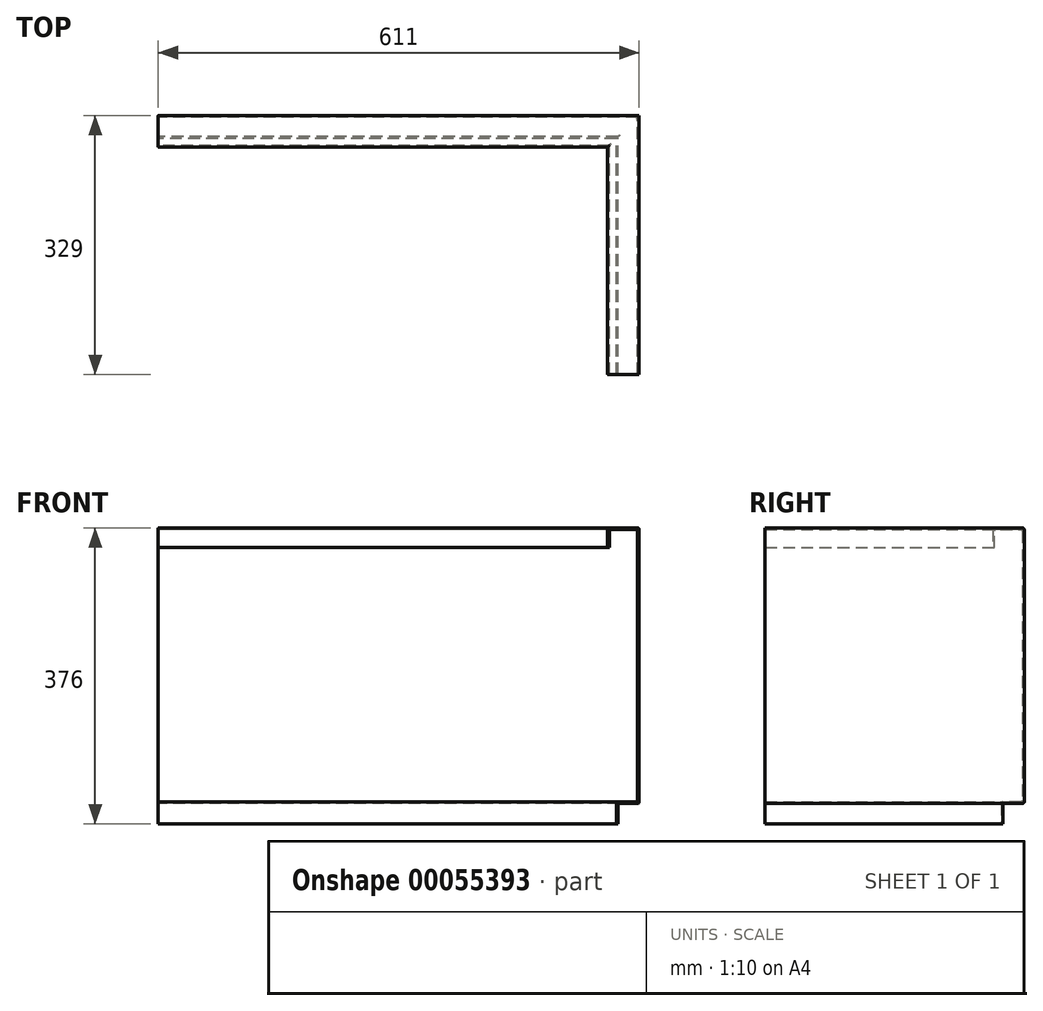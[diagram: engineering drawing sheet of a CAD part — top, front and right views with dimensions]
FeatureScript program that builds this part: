
annotation { "Feature Type Name" : "Feature", "Feature Type Description" : "" }
export const myFeature = defineFeature(function(context is Context, id is Id, definition is map)
    precondition{}
    {
        {
            var Q0;
            Q0=qCreatedBy(makeId("Front.planeOp"),FACE);
            var sketch = newSketch(context, id + "F0", { "sketchPlane" : qUnion([Q0])});
            skLineSegment(sketch, "E0", {"start": v(0, 0) * mm, "end": v(0, -350) * mm});
            skLineSegment(sketch, "E1", {"start": v(0, -350) * mm, "end": v(-27, -350) * mm});
            skLineSegment(sketch, "E2", {"start": v(-27, -350) * mm, "end": v(-27, -376) * mm});
            skLineSegment(sketch, "E3", {"start": v(0, 0) * mm, "end": v(-40, 0) * mm});
            skLineSegment(sketch, "E4", {"start": v(-40, 0) * mm, "end": v(-40, -25) * mm});
            skLineSegment(sketch, "E5.0", {"start": v(-38, -2) * mm, "end": v(-38, -25) * mm});
            skLineSegment(sketch, "E5.1", {"start": v(-29, -348) * mm, "end": v(-29, -376) * mm});
            skLineSegment(sketch, "E5.2", {"start": v(-2, -348) * mm, "end": v(-29, -348) * mm});
            skLineSegment(sketch, "E5.3", {"start": v(-2, -2) * mm, "end": v(-2, -348) * mm});
            skLineSegment(sketch, "E5.4", {"start": v(-2, -2) * mm, "end": v(-38, -2) * mm});
            skLineSegment(sketch, "E6", {"start": v(-40, -25) * mm, "end": v(-38, -25) * mm});
            skLineSegment(sketch, "E7", {"start": v(-29, -376) * mm, "end": v(-27, -376) * mm});
            skSolve(sketch);
        }
        {
            var Q0;
            Q0=qCreatedBy(makeId("Top.planeOp"),FACE);
            var sketch = newSketch(context, id + "F1", { "sketchPlane" : qUnion([Q0])});
            skLineSegment(sketch, "E8", {"start": v(0, 0) * mm, "end": v(0, 329) * mm});
            skLineSegment(sketch, "E9", {"start": v(-611, 329) * mm, "end": v(0, 329) * mm});
            skSolve(sketch);
        }
        {
            var Q0;
            Q0=qSketchRegion(id+"F0",true);
            var Q1;
            Q1=qConstructionFilter(qBodyType(qCreatedBy(id+"F1",EDGE),BodyType.WIRE),ConstructionObject.NO);
            sweep(context, id + "F2", {"profiles" : qUnion([Q0]), "path" : qUnion([Q1])});
        }
        {
            var Q0;
            Q0=makeQuery(id+"F2.opSweep","SWEPT_EDGE",EDGE,{"disambiguationData":[OSD([sQuery(id+"F0.wireOp",EDGE,"E3"),sQuery(id+"F0.wireOp",EDGE,"E4"),sQuery(id+"F1.wireOp",EDGE,"E9")])]});
            var Q1;
            Q1=makeQuery(id+"F2.opSweep","SWEPT_EDGE",EDGE,{"disambiguationData":[OSD([sQuery(id+"F0.wireOp",EDGE,"E0"),sQuery(id+"F0.wireOp",EDGE,"E3"),sQuery(id+"F1.wireOp",EDGE,"E9")])]});
            var Q2;
            Q2=makeQuery(id+"F2.opSweep","SWEPT_EDGE",EDGE,{"disambiguationData":[OSD([sQuery(id+"F0.wireOp",EDGE,"E3"),sQuery(id+"F0.wireOp",EDGE,"E4"),sQuery(id+"F1.wireOp",EDGE,"E8")])]});
            var Q3;
            Q3=makeQuery(id+"F2.opSweep","SWEPT_EDGE",EDGE,{"disambiguationData":[OSD([sQuery(id+"F0.wireOp",EDGE,"E0"),sQuery(id+"F0.wireOp",EDGE,"E3"),sQuery(id+"F1.wireOp",EDGE,"E8")])]});
            var Q4;
            Q4=makeQuery(id+"F2.opSweep","SWEPT_EDGE",EDGE,{"disambiguationData":[OSD([sQuery(id+"F0.wireOp",EDGE,"E5.2"),sQuery(id+"F0.wireOp",EDGE,"E5.3"),sQuery(id+"F1.wireOp",EDGE,"E9")])]});
            var Q5;
            Q5=makeQuery(id+"F2.opSweep","SWEPT_EDGE",EDGE,{"disambiguationData":[OSD([sQuery(id+"F0.wireOp",EDGE,"E5.1"),sQuery(id+"F0.wireOp",EDGE,"E5.2"),sQuery(id+"F1.wireOp",EDGE,"E9")])]});
            var Q6;
            Q6=makeQuery(id+"F2.opSweep","SWEPT_EDGE",EDGE,{"disambiguationData":[OSD([sQuery(id+"F0.wireOp",EDGE,"E5.1"),sQuery(id+"F0.wireOp",EDGE,"E5.2"),sQuery(id+"F1.wireOp",EDGE,"E8")])]});
            var Q7;
            Q7=makeQuery(id+"F2.opSweep","SWEPT_EDGE",EDGE,{"disambiguationData":[OSD([sQuery(id+"F0.wireOp",EDGE,"E5.2"),sQuery(id+"F0.wireOp",EDGE,"E5.3"),sQuery(id+"F1.wireOp",EDGE,"E8")])]});
            var Q8;
            Q8=makeQuery(id+"F2.opSweep","SWEPT_EDGE",EDGE,{"disambiguationData":[OSD([sQuery(id+"F0.wireOp",EDGE,"E0"),sQuery(id+"F0.wireOp",EDGE,"E1"),sQuery(id+"F1.wireOp",EDGE,"E8")])]});
            var Q9;
            Q9=makeQuery(id+"F2.opSweep","SWEPT_EDGE",EDGE,{"disambiguationData":[OSD([sQuery(id+"F0.wireOp",EDGE,"E1"),sQuery(id+"F0.wireOp",EDGE,"E2"),sQuery(id+"F1.wireOp",EDGE,"E8")])]});
            var Q10;
            Q10=makeQuery(id+"F2.opSweep","SWEPT_EDGE",EDGE,{"disambiguationData":[OSD([sQuery(id+"F0.wireOp",EDGE,"E1"),sQuery(id+"F0.wireOp",EDGE,"E2"),sQuery(id+"F1.wireOp",EDGE,"E9")])]});
            var Q11;
            Q11=makeQuery(id+"F2.opSweep","SWEPT_EDGE",EDGE,{"disambiguationData":[OSD([sQuery(id+"F0.wireOp",EDGE,"E0"),sQuery(id+"F0.wireOp",EDGE,"E1"),sQuery(id+"F1.wireOp",EDGE,"E9")])]});
            var Q12;
            Q12=makeQuery(id+"F2.opSweep","SWEPT_EDGE",EDGE,{"disambiguationData":[OSD([sQuery(id+"F0.wireOp",EDGE,"E5.3"),sQuery(id+"F0.wireOp",EDGE,"E5.4"),sQuery(id+"F1.wireOp",EDGE,"E9")])]});
            var Q13;
            Q13=makeQuery(id+"F2.opSweep","SWEPT_EDGE",EDGE,{"disambiguationData":[OSD([sQuery(id+"F0.wireOp",EDGE,"E5.3"),sQuery(id+"F0.wireOp",EDGE,"E5.4"),sQuery(id+"F1.wireOp",EDGE,"E8")])]});
            var Q14;
            Q14=makeQuery(id+"F2.opSweep","SWEPT_EDGE",EDGE,{"disambiguationData":[OSD([sQuery(id+"F0.wireOp",EDGE,"E5.0"),sQuery(id+"F0.wireOp",EDGE,"E5.4"),sQuery(id+"F1.wireOp",EDGE,"E8")])]});
            var Q15;
            Q15=makeQuery(id+"F2.opSweep","SWEPT_EDGE",EDGE,{"disambiguationData":[OSD([sQuery(id+"F0.wireOp",EDGE,"E5.0"),sQuery(id+"F0.wireOp",EDGE,"E5.4"),sQuery(id+"F1.wireOp",EDGE,"E9")])]});
            fillet(context, id + "F3", {"entities" : qUnion([Q0, Q1, Q2, Q3, Q4, Q5, Q6, Q7, Q8, Q9, Q10, Q11, Q12, Q13, Q14, Q15]), "radius" : 2 * mm, "tangentPropagation" : true, "allowEdgeOverflow" : false});
        }
    });
